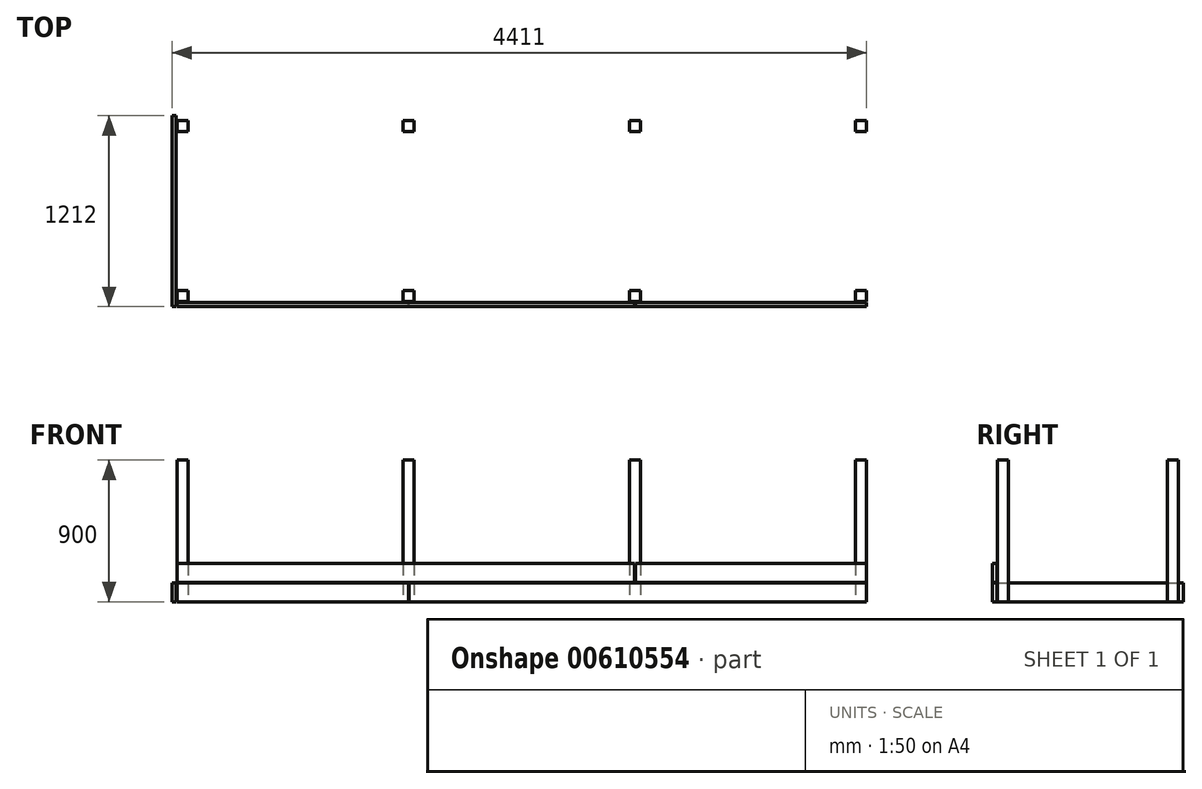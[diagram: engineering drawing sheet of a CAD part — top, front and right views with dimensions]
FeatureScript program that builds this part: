
annotation { "Feature Type Name" : "Feature", "Feature Type Description" : "" }
export const myFeature = defineFeature(function(context is Context, id is Id, definition is map)
    precondition{}
    {
        {
            var Q0;
            Q0=qCreatedBy(makeId("Top.planeOp"),FACE);
            var sketch = newSketch(context, id + "F0", { "sketchPlane" : qUnion([Q0])});
            skLineSegment(sketch, "E0.bottom", {"start": v(0, 0) * mm, "end": v(-4380, 0) * mm, "construction": true});
            skLineSegment(sketch, "E0.top", {"start": v(0, 1150) * mm, "end": v(-4380, 1150) * mm, "construction": true});
            skLineSegment(sketch, "E0.left", {"start": v(0, 0) * mm, "end": v(0, 1150) * mm, "construction": true});
            skLineSegment(sketch, "E0.right", {"start": v(-4380, 0) * mm, "end": v(-4380, 1150) * mm, "construction": true});
            skLineSegment(sketch, "E1", {"start": v(-4310, 1150) * mm, "end": v(-4310, 0) * mm, "construction": true});
            skLineSegment(sketch, "E2", {"start": v(-4380, 1080) * mm, "end": v(0, 1080) * mm, "construction": true});
            skLineSegment(sketch, "E3", {"start": v(-2190, 1150) * mm, "end": v(-2190, 0) * mm, "construction": true});
            skLineSegment(sketch, "E4", {"start": v(-2943.33, 1150) * mm, "end": v(-2943.33, 0) * mm, "construction": true});
            skLineSegment(sketch, "E5", {"start": v(-2873.33, 1150) * mm, "end": v(-2873.33, 0) * mm, "construction": true});
            skLineSegment(sketch, "E6", {"start": v(-4380, 575) * mm, "end": v(0, 575) * mm, "construction": true});
            skLineSegment(sketch, "E7.bottom", {"start": v(-2943.33, 1150) * mm, "end": v(-2873.33, 1150) * mm});
            skLineSegment(sketch, "E7.top", {"start": v(-2943.33, 1080) * mm, "end": v(-2873.33, 1080) * mm});
            skLineSegment(sketch, "E7.left", {"start": v(-2943.33, 1150) * mm, "end": v(-2943.33, 1080) * mm});
            skLineSegment(sketch, "E7.right", {"start": v(-2873.33, 1150) * mm, "end": v(-2873.33, 1080) * mm});
            skLineSegment(sketch, "E8.bottom", {"start": v(-4380, 1150) * mm, "end": v(-4310, 1150) * mm, "construction": true});
            skLineSegment(sketch, "E8.top", {"start": v(-4380, 1080) * mm, "end": v(-4310, 1080) * mm});
            skLineSegment(sketch, "E8.left", {"start": v(-4380, 1150) * mm, "end": v(-4380, 1080) * mm, "construction": true});
            skLineSegment(sketch, "E8.right", {"start": v(-4310, 1150) * mm, "end": v(-4310, 1080) * mm});
            skLineSegment(sketch, "E9.MirrorCS", {"start": v(-4380, 0) * mm, "end": v(-4380, 70) * mm, "construction": true});
            skLineSegment(sketch, "E10.MirrorCS", {"start": v(-2943.33, 0) * mm, "end": v(-2943.33, 70) * mm});
            skLineSegment(sketch, "E11.MirrorCS", {"start": v(-2943.33, 70) * mm, "end": v(-2873.33, 70) * mm});
            skLineSegment(sketch, "E12.MirrorCS", {"start": v(-2943.33, 0) * mm, "end": v(-2873.33, 0) * mm});
            skLineSegment(sketch, "E13.MirrorCS", {"start": v(-4380, 0) * mm, "end": v(-4310, 0) * mm, "construction": true});
            skLineSegment(sketch, "E14.MirrorCS", {"start": v(-4380, 70) * mm, "end": v(-4310, 70) * mm});
            skLineSegment(sketch, "E15.MirrorCS", {"start": v(-4310, 0) * mm, "end": v(-4310, 70) * mm});
            skLineSegment(sketch, "E16.MirrorCS", {"start": v(-2873.33, 0) * mm, "end": v(-2873.33, 70) * mm});
            skLineSegment(sketch, "E17.MirrorCS", {"start": v(-4380, 0) * mm, "end": v(-4310, 0) * mm});
            skLineSegment(sketch, "E18.MirrorCS", {"start": v(-4380, 1150) * mm, "end": v(-4310, 1150) * mm});
            skLineSegment(sketch, "E19.MirrorCS", {"start": v(0, 0) * mm, "end": v(-70, 0) * mm});
            skLineSegment(sketch, "E20.MirrorCS", {"start": v(-1506.67, 0) * mm, "end": v(-1506.67, 70) * mm});
            skLineSegment(sketch, "E21.MirrorCS", {"start": v(-1436.67, 0) * mm, "end": v(-1436.67, 70) * mm});
            skLineSegment(sketch, "E22.MirrorCS", {"start": v(-1436.67, 70) * mm, "end": v(-1506.67, 70) * mm});
            skLineSegment(sketch, "E23.MirrorCS", {"start": v(-70, 0) * mm, "end": v(-70, 70) * mm});
            skLineSegment(sketch, "E24.MirrorCS", {"start": v(-1436.67, 0) * mm, "end": v(-1506.67, 0) * mm});
            skLineSegment(sketch, "E25.MirrorCS", {"start": v(0, 70) * mm, "end": v(-70, 70) * mm});
            skLineSegment(sketch, "E26.MirrorCS", {"start": v(0, 0) * mm, "end": v(0, 70) * mm});
            skLineSegment(sketch, "E27.MirrorCS", {"start": v(0, 0) * mm, "end": v(-70, 0) * mm, "construction": true});
            skLineSegment(sketch, "E28.MirrorCS", {"start": v(-70, 1150) * mm, "end": v(-70, 1080) * mm});
            skLineSegment(sketch, "E29.MirrorCS", {"start": v(-1436.67, 1150) * mm, "end": v(-1506.67, 1150) * mm});
            skLineSegment(sketch, "E30.MirrorCS", {"start": v(-1436.67, 1150) * mm, "end": v(-1436.67, 1080) * mm});
            skLineSegment(sketch, "E31.MirrorCS", {"start": v(0, 1150) * mm, "end": v(0, 1080) * mm});
            skLineSegment(sketch, "E32.MirrorCS", {"start": v(-1436.67, 1080) * mm, "end": v(-1506.67, 1080) * mm});
            skLineSegment(sketch, "E33.MirrorCS", {"start": v(-1506.67, 1150) * mm, "end": v(-1506.67, 1080) * mm});
            skLineSegment(sketch, "E34.MirrorCS", {"start": v(0, 1150) * mm, "end": v(-70, 1150) * mm});
            skLineSegment(sketch, "E35.MirrorCS", {"start": v(0, 1080) * mm, "end": v(-70, 1080) * mm});
            skLineSegment(sketch, "E36.MirrorCS", {"start": v(-1436.67, 1150) * mm, "end": v(-1436.67, 0) * mm, "construction": true});
            skLineSegment(sketch, "E37.MirrorCS", {"start": v(-1506.67, 1150) * mm, "end": v(-1506.67, 0) * mm, "construction": true});
            skLineSegment(sketch, "E38", {"start": v(-4310, 575) * mm, "end": v(-2943.33, 575) * mm, "construction": true});
            skLineSegment(sketch, "E39", {"start": v(-2873.33, 575) * mm, "end": v(-1506.67, 575) * mm});
            skLineSegment(sketch, "E40", {"start": v(-2908.33, 1150) * mm, "end": v(-2908.33, 0) * mm, "construction": true});
            skLineSegment(sketch, "E41", {"start": v(-1471.67, 1150) * mm, "end": v(-1471.67, 0) * mm, "construction": true});
            skLineSegment(sketch, "E42.bottom", {"start": v(-4380, 70) * mm, "end": v(-4385, 70) * mm, "construction": true});
            skLineSegment(sketch, "E42.top", {"start": v(-4380, 0) * mm, "end": v(-4385, 0) * mm, "construction": true});
            skLineSegment(sketch, "E42.left", {"start": v(-4380, 70) * mm, "end": v(-4380, 0) * mm});
            skLineSegment(sketch, "E42.right", {"start": v(-4385, 70) * mm, "end": v(-4385, 0) * mm, "construction": true});
            skLineSegment(sketch, "E43.top", {"start": v(-4380, -5) * mm, "end": v(-4310, -5) * mm, "construction": true});
            skLineSegment(sketch, "E43.left", {"start": v(-4380, 0) * mm, "end": v(-4380, -5) * mm, "construction": true});
            skLineSegment(sketch, "E43.right", {"start": v(-4310, 0) * mm, "end": v(-4310, -5) * mm, "construction": true});
            skLineSegment(sketch, "E44.MirrorCS", {"start": v(-4310, 1150) * mm, "end": v(-4310, 1155) * mm, "construction": true});
            skLineSegment(sketch, "E45.MirrorCS", {"start": v(-4380, 1150) * mm, "end": v(-4385, 1150) * mm, "construction": true});
            skLineSegment(sketch, "E46.MirrorCS", {"start": v(-4380, 1150) * mm, "end": v(-4380, 1155) * mm, "construction": true});
            skLineSegment(sketch, "E47.MirrorCS", {"start": v(-4380, 1080) * mm, "end": v(-4385, 1080) * mm, "construction": true});
            skLineSegment(sketch, "E48.MirrorCS", {"start": v(-4385, 1080) * mm, "end": v(-4385, 1150) * mm, "construction": true});
            skLineSegment(sketch, "E49.MirrorCS", {"start": v(-4380, 1080) * mm, "end": v(-4380, 1150) * mm});
            skLineSegment(sketch, "E50.MirrorCS", {"start": v(-4380, 1155) * mm, "end": v(-4310, 1155) * mm, "construction": true});
            skLineSegment(sketch, "E51.bottom", {"start": v(-4385, 1182) * mm, "end": v(-4412, 1182) * mm});
            skLineSegment(sketch, "E51.top", {"start": v(-4385, -32) * mm, "end": v(-4412, -32) * mm, "construction": true});
            skLineSegment(sketch, "E51.left", {"start": v(-4385, 1182) * mm, "end": v(-4385, -32) * mm, "construction": true});
            skLineSegment(sketch, "E51.right", {"start": v(-4412, 1182) * mm, "end": v(-4412, -32) * mm, "construction": true});
            skLineSegment(sketch, "E52.bottom", {"start": v(-4380, -5) * mm, "end": v(-1471.67, -5) * mm, "construction": true});
            skLineSegment(sketch, "E52.top", {"start": v(-4380, -32) * mm, "end": v(-1471.67, -32) * mm, "construction": true});
            skLineSegment(sketch, "E52.left", {"start": v(-4380, -5) * mm, "end": v(-4380, -32) * mm, "construction": true});
            skLineSegment(sketch, "E52.right", {"start": v(-1471.67, -5) * mm, "end": v(-1471.67, -32) * mm, "construction": true});
            skLineSegment(sketch, "E53.MirrorCS", {"start": v(5, 1182) * mm, "end": v(32, 1182) * mm, "construction": true});
            skLineSegment(sketch, "E54.MirrorCS", {"start": v(32, 1182) * mm, "end": v(32, -32) * mm, "construction": true});
            skLineSegment(sketch, "E55.MirrorCS", {"start": v(5, -32) * mm, "end": v(32, -32) * mm, "construction": true});
            skLineSegment(sketch, "E56.MirrorCS", {"start": v(5, 1182) * mm, "end": v(5, -32) * mm, "construction": true});
            skLineSegment(sketch, "E57.bottom", {"start": v(-1471.67, -32) * mm, "end": v(0, -32) * mm, "construction": true});
            skLineSegment(sketch, "E57.top", {"start": v(-1471.67, -5) * mm, "end": v(0, -5) * mm, "construction": true});
            skLineSegment(sketch, "E57.left", {"start": v(-1471.67, -32) * mm, "end": v(-1471.67, -5) * mm, "construction": true});
            skLineSegment(sketch, "E57.right", {"start": v(0, -32) * mm, "end": v(0, -5) * mm, "construction": true});
            skSolve(sketch);
        }
        {
            var Q0;
            Q0 = qSketchRegion(id + "F0", true);
            extrude(context, id + "F1", {"entities" : qUnion([Q0]), "depth" : 900 * mm, "offsetDistance" : 25 * mm});
        }
        {
            var Q0;
            Q0=makeQuery(id+"F1.opExtrude","SWEPT_FACE",FACE,{"disambiguationData":[OSD([sQuery(id+"F0.wireOp",EDGE,"E17.MirrorCS")])]});
            var sketch = newSketch(context, id + "F2", { "sketchPlane" : qUnion([Q0])});
            skLineSegment(sketch, "E58", {"start": v(-4380, 450) * mm, "end": v(0, 450) * mm, "construction": true});
            skLineSegment(sketch, "E59", {"start": v(-2190, 450) * mm, "end": v(-2190, 928.3) * mm, "construction": true});
            skLineSegment(sketch, "E60", {"start": v(-2908.33, 900) * mm, "end": v(-2908.33, 0) * mm, "construction": true});
            skLineSegment(sketch, "E61", {"start": v(-2943.33, 900) * mm, "end": v(-2873.33, 900) * mm, "construction": true});
            skLineSegment(sketch, "E62.bottom", {"start": v(-2905.83, 900) * mm, "end": v(-2910.83, 900) * mm, "construction": true});
            skLineSegment(sketch, "E62.top", {"start": v(-2905.83, 0) * mm, "end": v(-2910.83, 0) * mm, "construction": true});
            skLineSegment(sketch, "E62.left", {"start": v(-2905.83, 900) * mm, "end": v(-2905.83, 0) * mm, "construction": true});
            skLineSegment(sketch, "E62.right", {"start": v(-2910.83, 900) * mm, "end": v(-2910.83, 0) * mm, "construction": true});
            skPoint(sketch, "E62.middle", {"position": v(-2908.33, 450) * mm});
            skLineSegment(sketch, "E63.MirrorCS", {"start": v(-1469.17, 900) * mm, "end": v(-1469.17, 0) * mm, "construction": true});
            skLineSegment(sketch, "E64.MirrorCS", {"start": v(-1474.17, 900) * mm, "end": v(-1474.17, 0) * mm, "construction": true});
            skLineSegment(sketch, "E65.bottom", {"start": v(-4380, 900) * mm, "end": v(-4385, 900) * mm, "construction": true});
            skLineSegment(sketch, "E65.top", {"start": v(-4380, 0) * mm, "end": v(-4385, 0) * mm, "construction": true});
            skLineSegment(sketch, "E65.left", {"start": v(-4380, 900) * mm, "end": v(-4380, 0) * mm, "construction": true});
            skLineSegment(sketch, "E65.right", {"start": v(-4385, 900) * mm, "end": v(-4385, 0) * mm, "construction": true});
            skLineSegment(sketch, "E66.bottom", {"start": v(-4385, 900) * mm, "end": v(-4411, 900) * mm, "construction": true});
            skLineSegment(sketch, "E66.top", {"start": v(-4385, 0) * mm, "end": v(-4411, 0) * mm, "construction": true});
            skLineSegment(sketch, "E66.right", {"start": v(-4411, 900) * mm, "end": v(-4411, 0) * mm, "construction": true});
            skLineSegment(sketch, "E67.MirrorCS", {"start": v(31, 900) * mm, "end": v(31, 0) * mm, "construction": true});
            skLineSegment(sketch, "E68.MirrorCS", {"start": v(5, 900) * mm, "end": v(5, 0) * mm, "construction": true});
            skLineSegment(sketch, "E69.bottom", {"start": v(-4380, 0) * mm, "end": v(-2910.83, 0) * mm});
            skLineSegment(sketch, "E69.top", {"start": v(-4380, 119) * mm, "end": v(-2910.83, 119) * mm});
            skLineSegment(sketch, "E69.left", {"start": v(-4380, 0) * mm, "end": v(-4380, 119) * mm});
            skLineSegment(sketch, "E69.right", {"start": v(-2910.83, 0) * mm, "end": v(-2910.83, 119) * mm});
            skLineSegment(sketch, "E70.bottom", {"start": v(-4380, 123) * mm, "end": v(-1474.17, 123) * mm});
            skLineSegment(sketch, "E70.top", {"start": v(-4380, 242) * mm, "end": v(-1474.17, 242) * mm});
            skLineSegment(sketch, "E70.left", {"start": v(-4380, 123) * mm, "end": v(-4380, 242) * mm});
            skLineSegment(sketch, "E70.right", {"start": v(-1474.17, 123) * mm, "end": v(-1474.17, 242) * mm});
            skLineSegment(sketch, "E71.bottom", {"start": v(-2905.83, 0) * mm, "end": v(0, 0) * mm});
            skLineSegment(sketch, "E71.top", {"start": v(-2905.83, 119) * mm, "end": v(0, 119) * mm});
            skLineSegment(sketch, "E71.left", {"start": v(-2905.83, 0) * mm, "end": v(-2905.83, 119) * mm});
            skLineSegment(sketch, "E71.right", {"start": v(0, 0) * mm, "end": v(0, 119) * mm});
            skLineSegment(sketch, "E72", {"start": v(-4277.43, 123) * mm, "end": v(-4277.43, 119) * mm, "construction": true});
            skLineSegment(sketch, "E73.bottom", {"start": v(-1469.17, 123) * mm, "end": v(0, 123) * mm});
            skLineSegment(sketch, "E73.top", {"start": v(-1469.17, 242) * mm, "end": v(0, 242) * mm});
            skLineSegment(sketch, "E73.left", {"start": v(-1469.17, 123) * mm, "end": v(-1469.17, 242) * mm});
            skLineSegment(sketch, "E73.right", {"start": v(0, 123) * mm, "end": v(0, 242) * mm});
            skSolve(sketch);
        }
        {
            var Q0;
            Q0 = qSketchRegion(id + "F2", true);
            extrude(context, id + "F3", {"entities" : qUnion([Q0]), "depth" : 31 * mm, "offsetDistance" : 25 * mm});
        }
        {
            var Q0;
            Q0=makeQuery(id+"F3.opExtrude","CAP_FACE",FACE,{"disambiguationData":[OSD([sQuery(id+"F2.wireOp",EDGE,"E69.bottom"),sQuery(id+"F2.wireOp",EDGE,"E69.top"),sQuery(id+"F2.wireOp",EDGE,"E69.left"),sQuery(id+"F2.wireOp",EDGE,"E69.right")])],"isStart":true});
            var sketch = newSketch(context, id + "F4", { "sketchPlane" : qUnion([Q0])});
            skLineSegment(sketch, "E74.bottom", {"start": v(-94.11, 1012.93) * mm, "end": v(4818.42, 1012.93) * mm});
            skLineSegment(sketch, "E74.top", {"start": v(-94.11, -245.8) * mm, "end": v(4818.42, -245.8) * mm});
            skLineSegment(sketch, "E74.left", {"start": v(-94.11, 1012.93) * mm, "end": v(-94.11, -245.8) * mm});
            skLineSegment(sketch, "E74.right", {"start": v(4818.42, 1012.93) * mm, "end": v(4818.42, -245.8) * mm});
            skSolve(sketch);
        }
        {
            var Q0;
            Q0 = qSketchRegion(id + "F4", true);
            extrude(context, id + "F5", {"entities" : qUnion([Q0]), "operationType" : NewBodyOperationType.REMOVE, "oppositeDirection" : true, "depth" : 5 * mm, "offsetDistance" : 25 * mm});
        }
        {
            var Q0;
            Q0=makeQuery(id+"F1.opExtrude","SWEPT_FACE",FACE,{"disambiguationData":[OSD([sQuery(id+"F0.wireOp",EDGE,"E42.left")])]});
            var sketch = newSketch(context, id + "F6", { "sketchPlane" : qUnion([Q0])});
            skLineSegment(sketch, "E75", {"start": v(0, 0) * mm, "end": v(-1150, 0) * mm, "construction": true});
            skLineSegment(sketch, "E76", {"start": v(-575, 0) * mm, "end": v(-575, 558.96) * mm, "construction": true});
            skPoint(sketch, "E76.endSnap0", {"position": v(-575, 0) * mm});
            skLineSegment(sketch, "E77.bottom", {"start": v(31, 0) * mm, "end": v(-1181, 0) * mm});
            skLineSegment(sketch, "E77.top", {"start": v(31, 119) * mm, "end": v(-1181, 119) * mm});
            skLineSegment(sketch, "E77.left", {"start": v(31, 0) * mm, "end": v(31, 119) * mm});
            skLineSegment(sketch, "E77.right", {"start": v(-1181, 0) * mm, "end": v(-1181, 119) * mm});
            skSolve(sketch);
        }
        {
            var Q0;
            Q0 = qSketchRegion(id + "F6", true);
            extrude(context, id + "F7", {"entities" : qUnion([Q0]), "depth" : 31 * mm, "offsetDistance" : 25 * mm});
        }
        {
            var Q0;
            Q0=makeQuery(id+"F7.opExtrude","CAP_FACE",FACE,{"disambiguationData":[OSD([sQuery(id+"F6.wireOp",EDGE,"E77.bottom"),sQuery(id+"F6.wireOp",EDGE,"E77.top"),sQuery(id+"F6.wireOp",EDGE,"E77.left"),sQuery(id+"F6.wireOp",EDGE,"E77.right")])],"isStart":true});
            var sketch = newSketch(context, id + "F8", { "sketchPlane" : qUnion([Q0])});
            skLineSegment(sketch, "E78.bottom", {"start": v(1181, 119) * mm, "end": v(-31, 119) * mm});
            skLineSegment(sketch, "E78.top", {"start": v(1181, 0) * mm, "end": v(-31, 0) * mm});
            skLineSegment(sketch, "E78.left", {"start": v(1181, 119) * mm, "end": v(1181, 0) * mm});
            skLineSegment(sketch, "E78.right", {"start": v(-31, 119) * mm, "end": v(-31, 0) * mm});
            skSolve(sketch);
        }
        {
            var Q0;
            Q0 = qSketchRegion(id + "F8", true);
            extrude(context, id + "F9", {"entities" : qUnion([Q0]), "operationType" : NewBodyOperationType.REMOVE, "oppositeDirection" : true, "depth" : 5 * mm, "offsetDistance" : 25 * mm});
        }
    });
